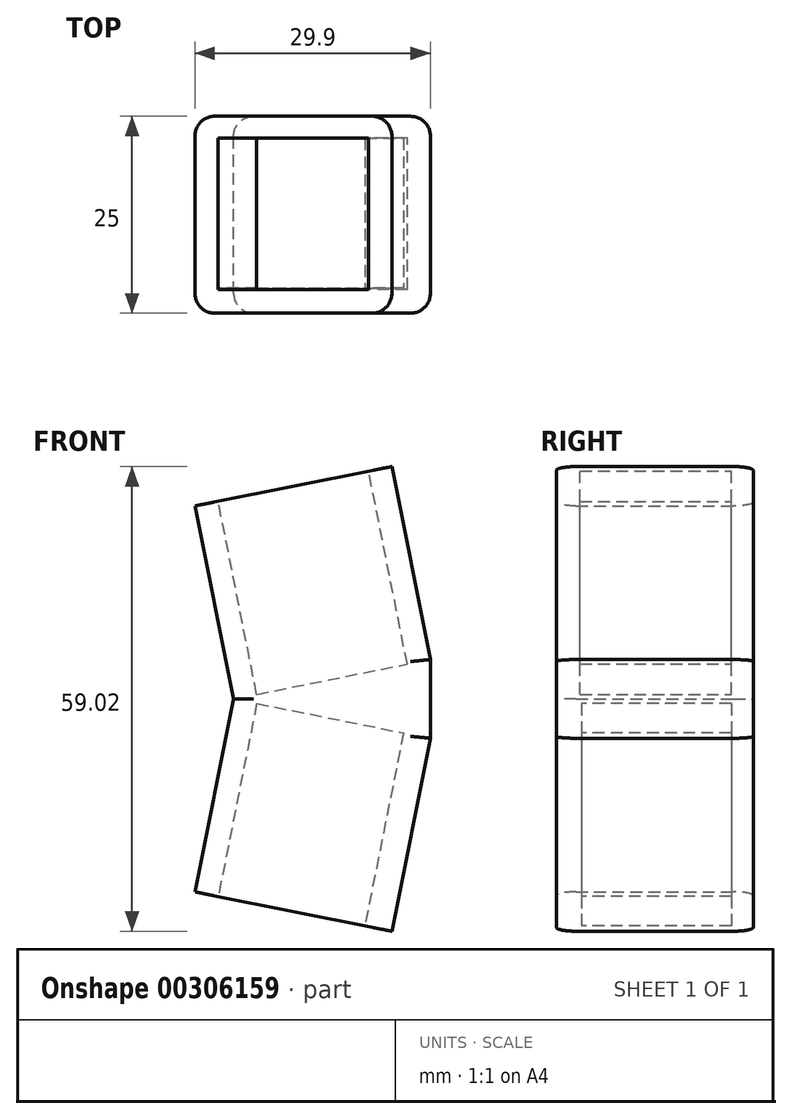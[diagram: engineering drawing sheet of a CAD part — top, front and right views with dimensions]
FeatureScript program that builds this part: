
annotation { "Feature Type Name" : "Feature", "Feature Type Description" : "" }
export const myFeature = defineFeature(function(context is Context, id is Id, definition is map)
    precondition{}
    {
        {
            var Q0;
            Q0=qCreatedBy(makeId("Top.planeOp"),FACE);
            var sketch = newSketch(context, id + "F0", { "sketchPlane" : qUnion([Q0])});
            skLineSegment(sketch, "E0.bottom", {"start": v(-25, 2.8) * mm, "end": v(0, 2.8) * mm});
            skLineSegment(sketch, "E0.top", {"start": v(-25, -22.2) * mm, "end": v(0, -22.2) * mm});
            skLineSegment(sketch, "E0.left", {"start": v(-25, 2.8) * mm, "end": v(-25, -22.2) * mm});
            skLineSegment(sketch, "E0.right", {"start": v(0, 2.8) * mm, "end": v(0, -22.2) * mm});
            skSolve(sketch);
        }
        {
            var Q0;
            Q0 = qSketchRegion(id + "F0", true);
            extrude(context, id + "F1", {"entities" : qUnion([Q0]), "depth" : 10 * mm});
        }
        {
            var Q0;
            Q0=makeQuery(id+"F1.opExtrude","CAP_EDGE",EDGE,{"disambiguationData":[OSD([sQuery(id+"F0.wireOp",EDGE,"E0.left")])],"isStart":false});
            chamfer(context, id + "F2", {"entities" : qUnion([Q0]), "chamferType" : ChamferType.TWO_OFFSETS, "width1" : 25 * mm, "oppositeDirection" : false, "width2" : 5 * mm});
        }
        {
            var Q0;
            Q0=makeQuery(id+"F1.opExtrude","CAP_EDGE",EDGE,{"disambiguationData":[OSD([sQuery(id+"F0.wireOp",EDGE,"E0.left")])],"isStart":true});
            chamfer(context, id + "F3", {"entities" : qUnion([Q0]), "chamferType" : ChamferType.TWO_OFFSETS, "width1" : 5 * mm, "oppositeDirection" : false, "width2" : 25 * mm, "tangentPropagation" : true});
        }
        {
            var Q0;
            Q0=makeQuery(id+"F2.opChamfer","BLEND_FACE",FACE,{"disambiguationData":[OSD([sQuery(id+"F0.wireOp",EDGE,"E0.left")])]});
            var sketch = newSketch(context, id + "F4", { "sketchPlane" : qUnion([Q0])});
            skLineSegment(sketch, "E1.bottom", {"start": v(-23.53, -22.2) * mm, "end": v(1.96, -22.2) * mm});
            skLineSegment(sketch, "E1.top", {"start": v(-23.53, 2.8) * mm, "end": v(1.96, 2.8) * mm});
            skLineSegment(sketch, "E1.left", {"start": v(-23.53, -22.2) * mm, "end": v(-23.53, 2.8) * mm});
            skLineSegment(sketch, "E1.right", {"start": v(1.96, -22.2) * mm, "end": v(1.96, 2.8) * mm});
            skSolve(sketch);
        }
        {
            var Q0;
            Q0 = qSketchRegion(id + "F4", true);
            extrude(context, id + "F5", {"entities" : qUnion([Q0]), "operationType" : NewBodyOperationType.ADD, "depth" : 25 * mm});
        }
        {
            var Q0;
            Q0=makeQuery(id+"F3.opChamfer","BLEND_FACE",FACE,{"disambiguationData":[OSD([sQuery(id+"F0.wireOp",EDGE,"E0.left")])]});
            extrude(context, id + "F6", {"entities" : qUnion([Q0]), "operationType" : NewBodyOperationType.ADD, "depth" : 25 * mm});
        }
        {
            var Q0;
            Q0=makeQuery(id+"F6.opExtrude","CAP_FACE",FACE,{"disambiguationData":[OSD([sQuery(id+"F0.wireOp",EDGE,"E0.left")])],"isStart":false});
            var sketch = newSketch(context, id + "F7", { "sketchPlane" : qUnion([Q0])});
            skLineSegment(sketch, "E2.bottom", {"start": v(-22.5, 0) * mm, "end": v(-3.5, 0) * mm});
            skLineSegment(sketch, "E2.top", {"start": v(-22.5, 19) * mm, "end": v(-3.5, 19) * mm});
            skLineSegment(sketch, "E2.left", {"start": v(-22.5, 0) * mm, "end": v(-22.5, 19) * mm});
            skLineSegment(sketch, "E2.right", {"start": v(-3.5, 0) * mm, "end": v(-3.5, 19) * mm});
            skSolve(sketch);
        }
        {
            var Q0;
            Q0 = qSketchRegion(id + "F7", true);
            extrude(context, id + "F8", {"entities" : qUnion([Q0]), "operationType" : NewBodyOperationType.REMOVE, "oppositeDirection" : true, "depth" : 25 * mm});
        }
        {
            var Q0;
            Q0=makeQuery(id+"F5.opExtrude","CAP_FACE",FACE,{"disambiguationData":[OSD([sQuery(id+"F4.wireOp",EDGE,"E1.bottom"),sQuery(id+"F4.wireOp",EDGE,"E1.top"),sQuery(id+"F4.wireOp",EDGE,"E1.left"),sQuery(id+"F4.wireOp",EDGE,"E1.right")])],"isStart":false});
            var sketch = newSketch(context, id + "F9", { "sketchPlane" : qUnion([Q0])});
            skLineSegment(sketch, "E3.bottom", {"start": v(-20.53, -19.2) * mm, "end": v(-1.04, -19.2) * mm});
            skLineSegment(sketch, "E3.top", {"start": v(-20.53, 0) * mm, "end": v(-1.04, 0) * mm});
            skLineSegment(sketch, "E3.left", {"start": v(-20.53, -19.2) * mm, "end": v(-20.53, 0) * mm});
            skLineSegment(sketch, "E3.right", {"start": v(-1.04, -19.2) * mm, "end": v(-1.04, 0) * mm});
            skSolve(sketch);
        }
        {
            var Q0;
            Q0 = qSketchRegion(id + "F9", true);
            extrude(context, id + "F10", {"entities" : qUnion([Q0]), "operationType" : NewBodyOperationType.REMOVE, "oppositeDirection" : true, "depth" : 25 * mm});
        }
        {
            var Q0;
            Q0=makeQuery(id+"F6.opExtrude","SWEPT_EDGE",EDGE,{"disambiguationData":[OSD([sQuery(id+"F0.wireOp",EDGE,"E0.top"),sQuery(id+"F0.wireOp",EDGE,"E0.left"),sQuery(id+"F4.wireOp",EDGE,"E1.bottom"),sQuery(id+"F4.wireOp",EDGE,"E1.left")])]});
            var Q1;
            Q1=makeQuery(id+"F5.opExtrude","SWEPT_EDGE",EDGE,{"disambiguationData":[OSD([sQuery(id+"F4.wireOp",EDGE,"E1.bottom"),sQuery(id+"F4.wireOp",EDGE,"E1.left")])]});
            fillet(context, id + "F11", {"entities" : qUnion([Q0, Q1]), "radius" : 2.5 * mm, "tangentPropagation" : true, "allowEdgeOverflow" : false});
        }
        {
            var Q0;
            Q0=makeQuery(id+"F6.opExtrude","SWEPT_EDGE",EDGE,{"disambiguationData":[OSD([sQuery(id+"F0.wireOp",EDGE,"E0.bottom"),sQuery(id+"F0.wireOp",EDGE,"E0.left"),sQuery(id+"F4.wireOp",EDGE,"E1.top"),sQuery(id+"F4.wireOp",EDGE,"E1.left")])]});
            var Q1;
            Q1=makeQuery(id+"F5.opExtrude","SWEPT_EDGE",EDGE,{"disambiguationData":[OSD([sQuery(id+"F4.wireOp",EDGE,"E1.top"),sQuery(id+"F4.wireOp",EDGE,"E1.left")])]});
            fillet(context, id + "F12", {"entities" : qUnion([Q0, Q1]), "radius" : 2.5 * mm, "tangentPropagation" : true, "allowEdgeOverflow" : false});
        }
        {
            var Q0;
            Q0=makeQuery(id+"F5.opExtrude","SWEPT_EDGE",EDGE,{"disambiguationData":[OSD([sQuery(id+"F4.wireOp",EDGE,"E1.bottom"),sQuery(id+"F4.wireOp",EDGE,"E1.right")])]});
            var Q1;
            Q1=makeQuery(id+"F1.opExtrude","SWEPT_EDGE",EDGE,{"disambiguationData":[OSD([sQuery(id+"F0.wireOp",EDGE,"E0.top"),sQuery(id+"F0.wireOp",EDGE,"E0.right")])]});
            var Q2;
            Q2=makeQuery(id+"F6.opExtrude","SWEPT_EDGE",EDGE,{"disambiguationData":[OSD([sQuery(id+"F0.wireOp",EDGE,"E0.top"),sQuery(id+"F0.wireOp",EDGE,"E0.left"),sQuery(id+"F0.wireOp",EDGE,"E0.right")])]});
            fillet(context, id + "F13", {"entities" : qUnion([Q0, Q1, Q2]), "radius" : 2.5 * mm, "tangentPropagation" : true, "allowEdgeOverflow" : false});
        }
        {
            var Q0;
            Q0=makeQuery(id+"F5.opExtrude","SWEPT_EDGE",EDGE,{"disambiguationData":[OSD([sQuery(id+"F4.wireOp",EDGE,"E1.top"),sQuery(id+"F4.wireOp",EDGE,"E1.right")])]});
            var Q1;
            Q1=makeQuery(id+"F1.opExtrude","SWEPT_EDGE",EDGE,{"disambiguationData":[OSD([sQuery(id+"F0.wireOp",EDGE,"E0.bottom"),sQuery(id+"F0.wireOp",EDGE,"E0.right")])]});
            var Q2;
            Q2=makeQuery(id+"F6.opExtrude","SWEPT_EDGE",EDGE,{"disambiguationData":[OSD([sQuery(id+"F0.wireOp",EDGE,"E0.bottom"),sQuery(id+"F0.wireOp",EDGE,"E0.left"),sQuery(id+"F0.wireOp",EDGE,"E0.right")])]});
            fillet(context, id + "F14", {"entities" : qUnion([Q0, Q1, Q2]), "radius" : 2.5 * mm, "tangentPropagation" : true, "allowEdgeOverflow" : false});
        }
    });
